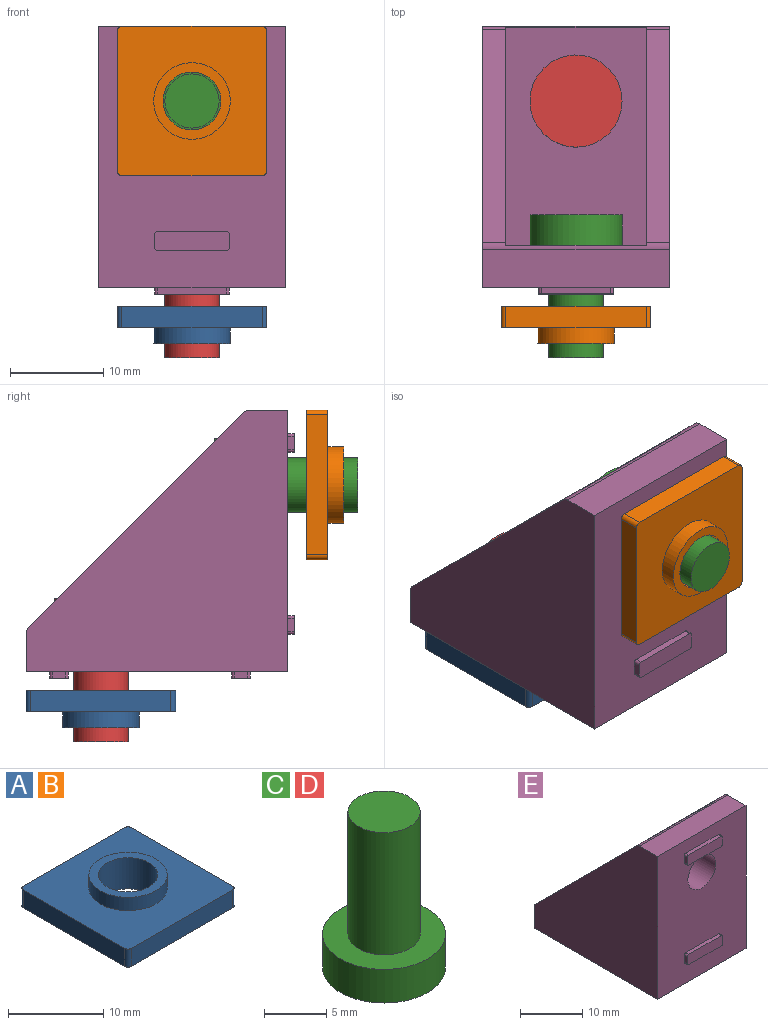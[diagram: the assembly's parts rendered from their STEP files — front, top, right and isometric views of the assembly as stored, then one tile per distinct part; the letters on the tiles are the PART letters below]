
ASSEMBLY  parts=5 mates=4
PART A: 13 faces, bbox 16x16x4 mm
  f0: plane 15x2.3mm, normal (0,1,0), area 34.5mm2, adj f1,f7,f8,f9
  f1: cylinder r=0.5mm len=2.3mm, axis (0,0,-1), area 1.8mm2, adj f0,f2,f8,f9
  f2: plane 15x2.3mm, normal (-1,0,0), area 34.5mm2, adj f1,f3,f8,f9
  f3: cylinder r=0.5mm len=2.3mm, axis (0,0,-1), area 1.8mm2, adj f2,f4,f8,f9
  f4: plane 15x2.3mm, normal (0,-1,0), area 34.5mm2, adj f3,f5,f8,f9
  f5: cylinder r=0.5mm len=2.3mm, axis (0,0,-1), area 1.8mm2, adj f4,f6,f8,f9
  f6: plane 15x2.3mm, normal (1,0,0), area 34.5mm2, adj f5,f7,f8,f9
  f7: cylinder r=0.5mm len=2.3mm, axis (0,0,-1), area 1.8mm2, adj f0,f6,f8,f9
  f8: plane 16x16mm, normal (0,0,1), area 203mm2, adj f0,f1,f2,f3,f4,f5,f6,f7
  f9: plane 16x16mm, normal (0,0,-1), area 225.6mm2, adj f0,f1,f2,f3,f4,f5,f6,f7
  f10: cylinder r=4.1mm len=8.2mm, axis (0,0,-1), area 43.8mm2, adj f8,f12
  f11: cylinder r=3.1mm len=6.2mm, axis (0,0,-1), area 77.9mm2, adj f9,f12
  f12: plane 8.2x8.2mm, normal (0,0,1), area 22.6mm2, adj f10,f11
PART B: same geometry as A
PART C: 5 faces, bbox 9.9x9.9x15.3 mm
  f0: cylinder r=4.94mm len=9.87mm, axis (0,0,1), area 102.3mm2, adj f1,f2
  f1: plane 9.87x9.87mm, normal (0,0,-1), area 76.5mm2, adj f0
  f2: plane 9.87x9.87mm, normal (0,0,1), area 50.1mm2, adj f0,f3
  f3: cylinder r=2.9mm len=12mm, axis (0,0,-1), area 218.7mm2, adj f2,f4
  f4: plane 5.8x5.8mm, normal (0,0,1), area 26.4mm2, adj f3
PART D: same geometry as C
PART E: 52 faces, bbox 20x28.7x28.7 mm
  f0: plane 23.41x15mm, normal (0,1,0), area 320mm2, adj f23,f27,f28,f32,f34
  f1: plane 20x4.09mm, normal (0,0,1), area 81.7mm2, adj f9,f25,f26,f27
  f2: plane 8x2mm, normal (0,-1,0), area 15.9mm2, adj f3,f4,f8,f10,f11,f12,f13,f14
  f3: plane 1.4x0.7mm, normal (-1,0,0), area 1mm2, adj f2,f4,f9,f14
  f4: cylinder r=0.3mm len=0.7mm, axis (0,-1,0), area 0.3mm2, adj f2,f3,f8,f9
  f5: plane 8x2mm, normal (0,0,-1), area 15.9mm2, adj f6,f7,f15,f17,f18,f19,f20,f21
  f6: cylinder r=0.3mm len=0.7mm, axis (0,0,-1), area 0.3mm2, adj f5,f7,f16,f21
  f7: plane 1.4x0.7mm, normal (-1,0,0), area 1mm2, adj f5,f6,f15,f16
  f8: plane 7.4x0.7mm, normal (0,0,1), area 5.2mm2, adj f2,f4,f9,f10
  f9: plane 28x20mm, normal (0,-1,0), area 497mm2, adj f1,f3,f4,f8,f10,f11,f12,f13
  f10: cylinder r=0.3mm len=0.7mm, axis (0,-1,0), area 0.3mm2, adj f2,f8,f9,f11
  f11: plane 1.4x0.7mm, normal (1,0,0), area 1mm2, adj f2,f9,f10,f12
  f12: cylinder r=0.3mm len=0.7mm, axis (0,-1,0), area 0.3mm2, adj f2,f9,f11,f13
  f13: plane 7.4x0.7mm, normal (0,0,-1), area 5.2mm2, adj f2,f9,f12,f14
  f14: cylinder r=0.3mm len=0.7mm, axis (0,-1,0), area 0.3mm2, adj f2,f3,f9,f13
  f15: cylinder r=0.3mm len=0.7mm, axis (0,0,-1), area 0.3mm2, adj f5,f7,f16,f17
  f16: plane 28x20mm, normal (0,0,-1), area 497mm2, adj f6,f7,f9,f15,f17,f18,f19,f20
  f17: plane 7.4x0.7mm, normal (0,-1,0), area 5.2mm2, adj f5,f15,f16,f18
  f18: cylinder r=0.3mm len=0.7mm, axis (0,0,-1), area 0.3mm2, adj f5,f16,f17,f19
  f19: plane 1.4x0.7mm, normal (1,0,0), area 1mm2, adj f5,f16,f18,f20
  f20: cylinder r=0.3mm len=0.7mm, axis (0,0,-1), area 0.3mm2, adj f5,f16,f19,f21
  f21: plane 7.4x0.7mm, normal (0,1,0), area 5.2mm2, adj f5,f6,f16,f20
  f22: cylinder r=0.3mm len=0.7mm, axis (0,0,-1), area 0.3mm2, adj f16,f44,f45,f50
  f23: plane 23.41x15mm, normal (0,0,1), area 320mm2, adj f0,f28,f30,f32,f33
  f24: plane 22.91x22.91mm, normal (0,0.71,0.71), area 81mm2, adj f26,f27,f30,f32
  f25: plane 28x28mm, normal (1,0,0), area 507.8mm2, adj f1,f9,f16,f27,f29,f30,f31
  f26: plane 28x28mm, normal (-1,0,0), area 507.8mm2, adj f1,f9,f16,f24,f27,f30,f31
  f27: cylinder r=1mm len=20mm, axis (1,0,0), area 10.3mm2, adj f0,f1,f24,f25,f26,f28,f29,f32
  f28: plane 23.41x23.41mm, normal (-1,0,0), area 276.1mm2, adj f0,f23,f27,f29,f30
  f29: plane 22.91x22.91mm, normal (0,0.71,0.71), area 81mm2, adj f25,f27,f28,f30
  f30: cylinder r=1mm len=20mm, axis (1,0,0), area 10.3mm2, adj f23,f24,f25,f26,f28,f29,f31,f32
  f31: plane 20x4.09mm, normal (0,1,0), area 81.7mm2, adj f16,f25,f26,f30
  f32: plane 23.41x23.41mm, normal (1,0,0), area 276.1mm2, adj f0,f23,f24,f27,f30
  f33: cylinder r=3.15mm len=6.3mm, axis (0,0,1), area 89.1mm2, adj f16,f23
  f34: cylinder r=3.15mm len=6.3mm, axis (0,1,0), area 89.1mm2, adj f0,f9
  f35: plane 1.4x0.7mm, normal (-1,0,0), area 1mm2, adj f9,f36,f42,f51
  f36: cylinder r=0.3mm len=0.7mm, axis (0,-1,0), area 0.3mm2, adj f9,f35,f37,f51
  f37: plane 7.4x0.7mm, normal (0,0,1), area 5.2mm2, adj f9,f36,f38,f51
  f38: cylinder r=0.3mm len=0.7mm, axis (0,-1,0), area 0.3mm2, adj f9,f37,f39,f51
  f39: plane 1.4x0.7mm, normal (1,0,0), area 1mm2, adj f9,f38,f40,f51
  f40: cylinder r=0.3mm len=0.7mm, axis (0,-1,0), area 0.3mm2, adj f9,f39,f41,f51
  f41: plane 7.4x0.7mm, normal (0,0,-1), area 5.2mm2, adj f9,f40,f42,f51
  f42: cylinder r=0.3mm len=0.7mm, axis (0,-1,0), area 0.3mm2, adj f9,f35,f41,f51
  f43: cylinder r=0.3mm len=0.7mm, axis (0,0,-1), area 0.3mm2, adj f16,f44,f49,f50
  f44: plane 1.4x0.7mm, normal (-1,0,0), area 1mm2, adj f16,f22,f43,f50
  f45: plane 7.4x0.7mm, normal (0,-1,0), area 5.2mm2, adj f16,f22,f46,f50
  f46: cylinder r=0.3mm len=0.7mm, axis (0,0,-1), area 0.3mm2, adj f16,f45,f47,f50
  f47: plane 1.4x0.7mm, normal (1,0,0), area 1mm2, adj f16,f46,f48,f50
  f48: cylinder r=0.3mm len=0.7mm, axis (0,0,-1), area 0.3mm2, adj f16,f47,f49,f50
  f49: plane 7.4x0.7mm, normal (0,1,0), area 5.2mm2, adj f16,f43,f48,f50
  f50: plane 8x2mm, normal (0,0,-1), area 15.9mm2, adj f22,f43,f44,f45,f46,f47,f48,f49
  f51: plane 8x2mm, normal (0,-1,0), area 15.9mm2, adj f35,f36,f37,f38,f39,f40,f41,f42
PLACE A rot(axis=(1,0,0),180deg) t=(-47.53,20.73,0.65)mm
PLACE B rot(axis=(1,0,0),90deg) t=(-47.53,-9.27,14.65)mm
PLACE C rot(axis=(1,0,0),90deg) t=(-20.48,-2.77,17.57)mm
PLACE D rot(axis=(1,0,0),180deg) t=(-20.48,17.81,7.15)mm
PLACE E t=(-7.78,-7.27,2.65)mm
MATE fastened A.f10 <-> E.f33  axis (0,0,1) through (-7.78,12.73,0.65)mm
MATE fastened C.f0 <-> E.f34  axis (0,-1,0) through (-7.78,-2.77,22.65)mm
MATE fastened D.f0 <-> E.f33  axis (0,0,-1) through (-7.78,12.73,7.15)mm
MATE fastened B.f10 <-> E.f34  axis (0,1,0) through (-7.78,-9.27,22.65)mm
